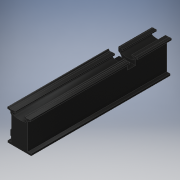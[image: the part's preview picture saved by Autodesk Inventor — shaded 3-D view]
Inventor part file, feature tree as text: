
AUTODESK INVENTOR PART (.ipt)
format: ipt  version: 2018 (Build 220112000, 112)  size: 456,192 bytes
history: native  units: in
note: dims shown in document units (in); Inventor stores cm internally (conversion verified against a paired STEP export)
features: sketch x13, extrude x12, reference x6, plane x3, chamfer x1
ambient origin geometry x8: Origin, YZ Plane, XZ Plane, XY Plane, X Axis, Y Axis, Z Axis, Center Point
bodies: Solid1 (feature_tree)
feature tree (35):
  extrude  "Extrusion1"  TaperAngle=150.0deg  [1 undecoded]
  chamfer  "Chamfer1"  Distance=0.5787in
  plane  "Work Plane3"
  extrude  "Extrusion2"  Depth=0.3937in
  extrude  "Extrusion3"  TaperAngle=120.0deg  [1 undecoded]
  extrude  "Extrusion4"  Depth=0.1575in
  extrude  "Extrusion5"  Depth=0.3937in
  extrude  "Extrusion6"  Depth=0.3937in
  extrude  "Extrusion7"  Depth=0.3937in
  extrude  "Extrusion8"  Depth=0.3937in
  plane  "Work Plane4"
  plane  "Work Plane5"
  extrude  "Extrusion9"  Depth=0.3937in
  extrude  "Extrusion10"  TaperAngle=180.0deg  [1 undecoded]
  extrude  "Extrusion11"  Depth=0.3937in
  extrude  "Extrusion12"  Depth=0.3937in
  sketch  "Sketch14"  dims[d13=0.6181in d14=0.5787in d15=0.315in d16=120.0deg d17=0.1575in d18=2.4409in d19=8.0315in d22=3.6299in d24=0.5in d25=1.4252in d26=180.0deg d27=0.0787in d28=0.748in d29=0.0787in d30=0.5197in d31=0.962in d32=0.1811in d33=0.6299in d34=0.962in d35=0.5512in d36=0.5512in d37=90.0deg d38=0.1181in d39=60.0deg d40=0.685in d41=0.8858in d43=5.2953in d44=90.0deg d46=2.185in d47=90.0deg d50=90.0deg d51=1.378in d52=180.0deg d53=0.7087in d54=90.0deg d55=1.378in d57=0.7087in d59=180.0deg d60=0.315in d61=120.0deg d62=2.4409in d63=55.9055in d64=0.0in d65=0.1575in d66=0.0787in d67=45.0deg d68=40.1575in d69=3.2283in d70=3.4528in d71=55.9055in d72=0.0in d73=55.9055in d74=0.0in d75=55.9055in d76=0.0in d77=3.3465in d78=1.2205in d79=1.7323in d80=55.9055in d81=0.0in d82=1.0236in d83=0.0in d84=0.315in d85=0.315in d86=0.7283in d87=0.5512in d88=0.5118in d89=0.3937in d90=0.0in d91=0.315in d92=0.315in d93=6.7717in d94=0.8858in d95=0.5512in d96=0.7874in d97=0.0in d98=0.2756in d99=0.3937in d100=0.0in d101=5.5118in d102=1.9685in d103=0.2756in d104=1.5748in d105=0.0787in d106=0.0in d107=0.7874in d108=0.0in d112=0.315in d113=1.9685in d114=0.0in d115=0.0in]
  sketch  "Sketch1"  dims[d0=0.4331in d1=150.0deg]
  sketch  "Sketch2"  dims[d2=0.3937in]
  sketch  "Sketch3"  dims[d3=0.4606in]
  sketch  "Sketch4"  dims[d4=0.4961in]
  sketch  "Sketch5"  dims[d5=0.962in]
  sketch  "Sketch6"  dims[d6=0.1496in]
  sketch  "Sketch8"  dims[d7=0.4016in]
  sketch  "Sketch9"  dims[d8=0.962in]
  sketch  "Sketch10"  dims[d9=0.126in]
  sketch  "Sketch11"  dims[d10=0.6339in]
  sketch  "Sketch12"  dims[d11=0.0787in]
  reference  "Reference1"
  reference  "Reference2"
  reference  "Reference3"
  reference  "Reference4"
  reference  "Reference5"
  reference  "Reference6"
  sketch  "Sketch13"  dims[d12=0.9921in]
note: 3 required parameter values undecoded (feature->parameter linkage not recoverable at this tier; creation-order binding heuristic only, values carry confidence <= 0.55)
